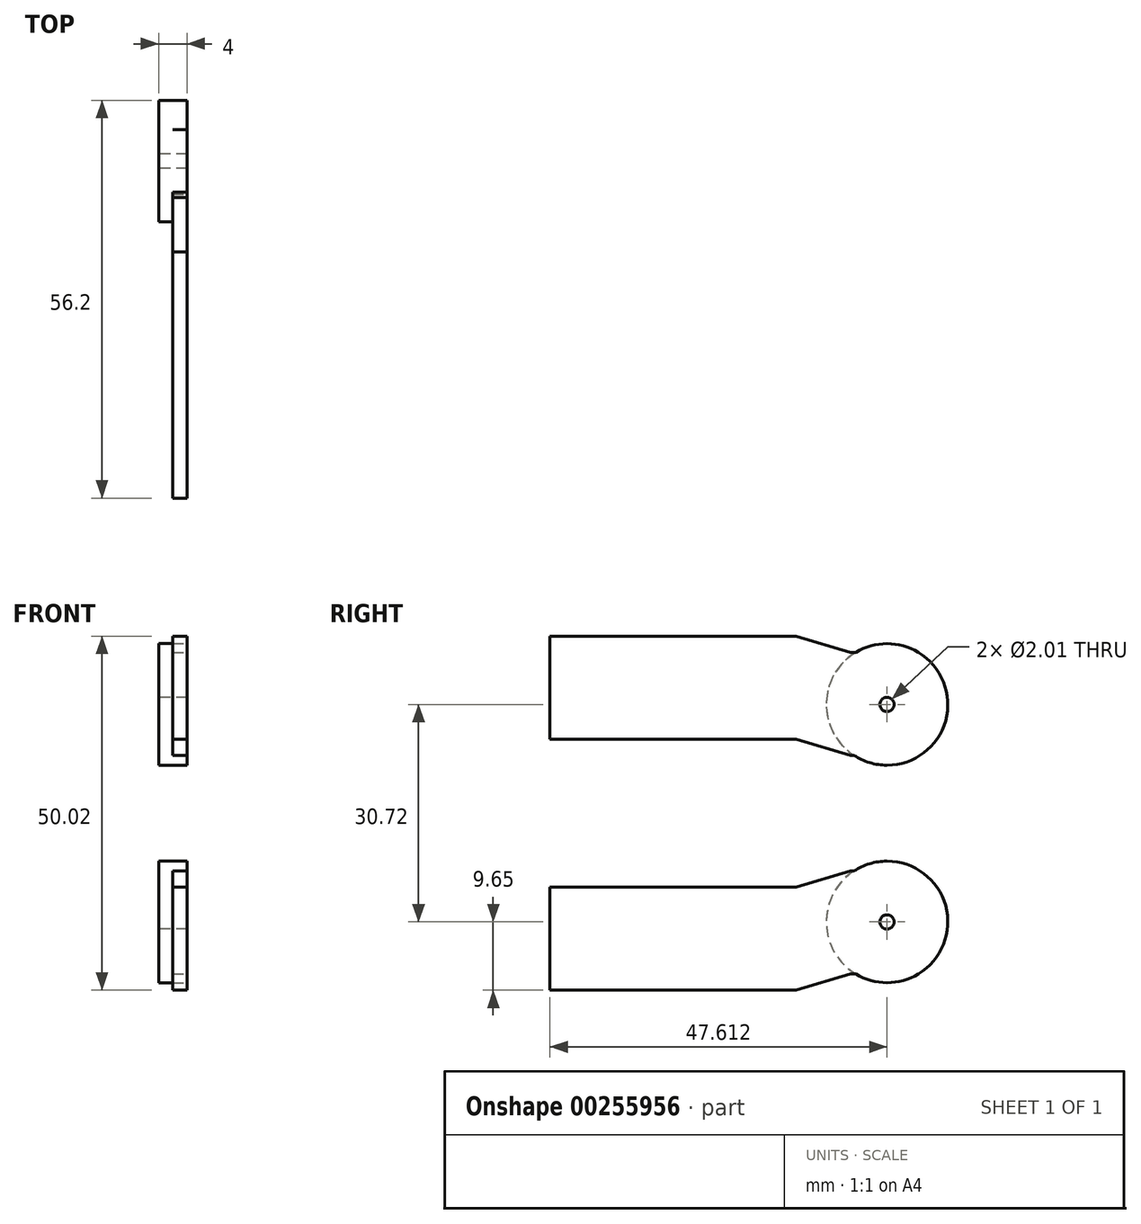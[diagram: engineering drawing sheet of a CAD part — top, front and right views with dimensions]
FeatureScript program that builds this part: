
annotation { "Feature Type Name" : "Feature", "Feature Type Description" : "" }
export const myFeature = defineFeature(function(context is Context, id is Id, definition is map)
    precondition{}
    {
        {
            var Q0;
            Q0=qCreatedBy(makeId("Right.planeOp"),FACE);
            var sketch = newSketch(context, id + "F0", { "sketchPlane" : qUnion([Q0])});
            skLineSegment(sketch, "E0.bottom", {"start": v(-8.44, 25.01) * mm, "end": v(26.36, 25.01) * mm});
            skLineSegment(sketch, "E0.top", {"start": v(-8.44, 10.46) * mm, "end": v(26.36, 10.46) * mm});
            skLineSegment(sketch, "E0.left", {"start": v(-8.44, 25.01) * mm, "end": v(-8.44, 10.46) * mm});
            skLineSegment(sketch, "E0.right", {"start": v(26.36, 25.01) * mm, "end": v(26.36, 10.46) * mm});
            skLineSegment(sketch, "E1", {"start": v(26.36, 25.01) * mm, "end": v(34.04, 22.72) * mm});
            skLineSegment(sketch, "E2", {"start": v(34.04, 22.72) * mm, "end": v(43.6, 22.72) * mm});
            skLineSegment(sketch, "E3", {"start": v(26.36, 10.46) * mm, "end": v(34.04, 8.17) * mm});
            skLineSegment(sketch, "E4", {"start": v(34.04, 8.17) * mm, "end": v(43.6, 8.17) * mm});
            skLineSegment(sketch, "E5", {"start": v(43.6, 8.17) * mm, "end": v(43.6, 22.72) * mm});
            skSolve(sketch);
        }
        {
            var Q0;
            Q0=makeQuery(id+"F0.imprint","IMPRINT",FACE,{"disambiguationData":[TD([[makeQuery(id+"F0.imprint","IMPRINT",EDGE,{"derivedFrom":sQuery(id+"F0.wireOp",EDGE,"E0.bottom")}),-1.0]])]});
            extrude(context, id + "F1", {"entities" : qUnion([Q0]), "oppositeDirection" : true, "depth" : 2 * mm});
        }
        {
            var Q0;
            Q0 = qSketchRegion(id + "F0", true);
            extrude(context, id + "F2", {"entities" : qUnion([Q0]), "operationType" : NewBodyOperationType.ADD, "oppositeDirection" : true, "depth" : 2 * mm});
        }
        {
            var Q0;
            Q0=qCreatedBy(makeId("Right.planeOp"),FACE);
            var sketch = newSketch(context, id + "F3", { "sketchPlane" : qUnion([Q0])});
            skCircle(sketch, "E6", {"center": v(39.17, 15.36) * mm, "radius": 8.58 * mm});
            skSolve(sketch);
        }
        {
            var Q0;
            Q0=makeQuery(id+"F3.imprint","IMPRINT",FACE,{"disambiguationData":[TD([[makeQuery(id+"F3.imprint","IMPRINT",EDGE,{"derivedFrom":sQuery(id+"F3.wireOp",EDGE,"E6")}),1.0]])]});
            extrude(context, id + "F4", {"entities" : qUnion([Q0]), "operationType" : NewBodyOperationType.ADD, "oppositeDirection" : true, "depth" : 4 * mm});
        }
        {
            var Q0;
            Q0=makeQuery(id+"F4.opExtrude","CAP_FACE",FACE,{"disambiguationData":[OSD([sQuery(id+"F3.wireOp",EDGE,"E6")])],"isStart":false});
            var sketch = newSketch(context, id + "F5", { "sketchPlane" : qUnion([Q0])});
            skCircle(sketch, "E7", {"center": v(-39.17, 15.36) * mm, "radius": 1 * mm});
            skSolve(sketch);
        }
        {
            var Q0;
            Q0=makeQuery(id+"F5.imprint","IMPRINT",FACE,{"disambiguationData":[TD([[makeQuery(id+"F5.imprint","IMPRINT",EDGE,{"derivedFrom":sQuery(id+"F5.wireOp",EDGE,"E7")}),1.0]])]});
            extrude(context, id + "F6", {"entities" : qUnion([Q0]), "operationType" : NewBodyOperationType.REMOVE, "oppositeDirection" : true, "depth" : 4 * mm});
        }
        {
            var Q0;
            Q0=makeQuery(id+"F1.opExtrude","SWEPT_BODY",BODY,{"disambiguationData":[OSD([sQuery(id+"F0.wireOp",EDGE,"E0.bottom"),sQuery(id+"F0.wireOp",EDGE,"E0.top"),sQuery(id+"F0.wireOp",EDGE,"E0.left"),sQuery(id+"F0.wireOp",EDGE,"E0.right")])]});
            var Q1;
            Q1=qCreatedBy(makeId("Top.planeOp"),FACE);
            mirror(context, id + "F7", {"entities" : qUnion([Q0]), "mirrorPlane" : qUnion([Q1])});
        }
    });
